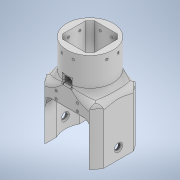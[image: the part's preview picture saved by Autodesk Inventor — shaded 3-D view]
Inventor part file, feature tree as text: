
AUTODESK INVENTOR PART (.ipt)
format: ipt  version: 2021 (Build 250183000, 183)  size: 825,344 bytes
history: native  units: mm
features: extrude x14, sketch x14, fillet x12, other x1
ambient origin geometry x8: Origin, YZ Plane, XZ Plane, XY Plane, X Axis, Y Axis, Z Axis, Center Point
bodies: Body1 (feature_tree)
feature tree (41):
  other  "Sólido1"
  extrude  "Extrusión1"  Depth=8.0mm
  extrude  "Extrusión2"  Depth=2.0mm
  fillet  "Empalme1"  Radius=400.0mm
  extrude  "Extrusión3"  Depth=40.0mm TaperAngle=0.0deg
  extrude  "Extrusión4"  Depth=12.0mm TaperAngle=0.0deg
  extrude  "Extrusión5"  Depth=160.0mm TaperAngle=0.0deg
  extrude  "Extrusión7"  Depth=2.0mm
  extrude  "Extrusión8"  Depth=50.0mm TaperAngle=0.0deg
  extrude  "Extrusión9"  Depth=10.0mm
  fillet  "Empalme2"  Radius=10.0mm
  fillet  "Empalme3"  Radius=10.0mm
  extrude  "Extrusión10"  Depth=10.0mm
  extrude  "Extrusión11"  Depth=10.0mm
  fillet  "Empalme4"  Radius=3.0mm
  fillet  "Empalme5"  Radius=500.0mm
  fillet  "Empalme6"  Radius=3.0mm
  fillet  "Empalme7"  Radius=3.0mm
  fillet  "Empalme8"  Radius=500.0mm
  fillet  "Empalme9"  Radius=3.0mm
  fillet  "Empalme10"  Radius=3.0mm
  extrude  "Extrusión12"  Depth=3.0mm
  extrude  "Extrusión13"  Depth=5.0mm
  extrude  "Extrusión14"  Depth=10.0mm
  extrude  "Extrusión15"  Depth=2.0mm
  fillet  "Empalme11"  Radius=2.0mm
  fillet  "Empalme12"  [1 undecoded]
  sketch  "Boceto1"  dims[d7=40.0mm d8=0.0mm d10=8.0mm]
  sketch  "Boceto2"  dims[d11=400.0mm d12=0.0mm d13=2.0mm d16=400.0mm d17=0.0mm]
  sketch  "Boceto3"  dims[d18=400.0mm d19=0.0mm d20=40.0mm d21=0.0mm]
  sketch  "Boceto4"  dims[d25=62.249mm d26=0.0mm d27=12.0mm d28=0.0mm]
  sketch  "Boceto5"  dims[d32=9.0mm d37=160.0mm d38=0.0mm]
  sketch  "Boceto8"  dims[d39=2.0mm d40=2.0mm]
  sketch  "Boceto9"  dims[d47=160.0mm d48=0.0mm d49=50.0mm d50=0.0mm]
  sketch  "Boceto13"  dims[d51=10.0mm d52=10.0mm d53=10.0mm d54=10.0mm]
  sketch  "Boceto15"  dims[d55=10.0mm d56=10.0mm]
  sketch  "Boceto16"  dims[d57=10.0mm d62=3.0mm d63=3.0mm d64=500.0mm d65=0.0mm d70=3.0mm d71=3.0mm d72=500.0mm d73=0.0mm d79=3.0mm d80=3.0mm]
  sketch  "Boceto17"  dims[d81=3.0mm d82=3.0mm]
  sketch  "Boceto18"  dims[d83=15.0mm d84=0.0mm d87=5.0mm]
  sketch  "Boceto20"  dims[d88=10.0mm d90=10.0mm]
  sketch  "Boceto21"  dims[d91=15.0mm d92=0.0mm d93=2.0mm d94=2.0mm]
note: 1 required parameter value undecoded (feature->parameter linkage not recoverable at this tier; creation-order binding heuristic only, values carry confidence <= 0.55)
